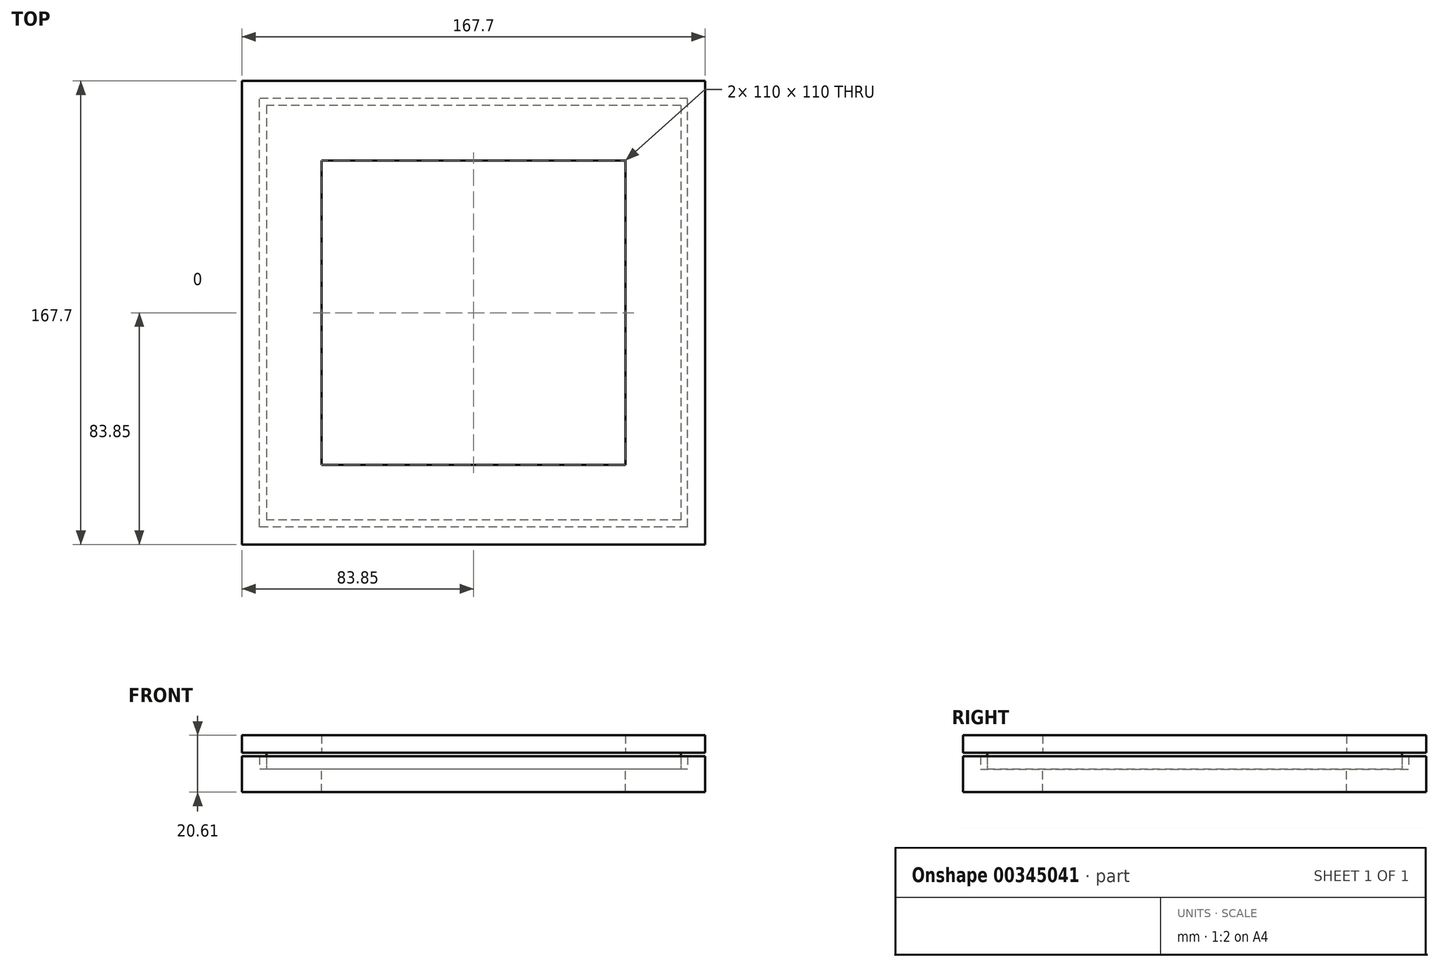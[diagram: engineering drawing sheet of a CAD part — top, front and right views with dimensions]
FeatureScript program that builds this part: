
annotation { "Feature Type Name" : "Feature", "Feature Type Description" : "" }
export const myFeature = defineFeature(function(context is Context, id is Id, definition is map)
    precondition{}
    {
        {
            var Q0;
            Q0=qCreatedBy(makeId("Top.planeOp"),FACE);
            var sketch = newSketch(context, id + "F0", { "sketchPlane" : qUnion([Q0])});
            skLineSegment(sketch, "E0.bottom", {"start": v(75, 75) * mm, "end": v(-75, 75) * mm});
            skLineSegment(sketch, "E0.top", {"start": v(75, -75) * mm, "end": v(-75, -75) * mm});
            skLineSegment(sketch, "E0.left", {"start": v(75, 75) * mm, "end": v(75, -75) * mm});
            skLineSegment(sketch, "E0.right", {"start": v(-75, 75) * mm, "end": v(-75, -75) * mm});
            skPoint(sketch, "E0.middle", {"position": v(0, 0) * mm});
            skSolve(sketch);
        }
        {
            var Q0;
            Q0 = qSketchRegion(id + "F0", true);
            extrude(context, id + "F1", {"entities" : qUnion([Q0]), "depth" : 6 * mm});
        }
        {
            var Q0;
            Q0=makeQuery(id+"F1.opExtrude","CAP_FACE",FACE,{"disambiguationData":[OSD([sQuery(id+"F0.wireOp",EDGE,"E0.bottom"),sQuery(id+"F0.wireOp",EDGE,"E0.top"),sQuery(id+"F0.wireOp",EDGE,"E0.left"),sQuery(id+"F0.wireOp",EDGE,"E0.right")])],"isStart":true});
            var sketch = newSketch(context, id + "F2", { "sketchPlane" : qUnion([Q0])});
            skLineSegment(sketch, "E1.bottom", {"start": v(55, 55) * mm, "end": v(-55, 55) * mm});
            skLineSegment(sketch, "E1.top", {"start": v(55, -55) * mm, "end": v(-55, -55) * mm});
            skLineSegment(sketch, "E1.left", {"start": v(55, 55) * mm, "end": v(55, -55) * mm});
            skLineSegment(sketch, "E1.right", {"start": v(-55, 55) * mm, "end": v(-55, -55) * mm});
            skPoint(sketch, "E1.middle", {"position": v(0, 0) * mm});
            skLineSegment(sketch, "E2.bottom", {"start": v(77.5, 77.5) * mm, "end": v(-77.5, 77.5) * mm});
            skLineSegment(sketch, "E2.top", {"start": v(77.5, -77.5) * mm, "end": v(-77.5, -77.5) * mm});
            skLineSegment(sketch, "E2.left", {"start": v(77.5, 77.5) * mm, "end": v(77.5, -77.5) * mm});
            skLineSegment(sketch, "E2.right", {"start": v(-77.5, 77.5) * mm, "end": v(-77.5, -77.5) * mm});
            skSolve(sketch);
        }
        {
            var Q0;
            Q0 = qSketchRegion(id + "F2", true);
            extrude(context, id + "F3", {"entities" : qUnion([Q0]), "depth" : 8.25 * mm});
        }
        {
            var Q0;
            Q0=makeQuery(id+"F3.opExtrude","CAP_FACE",FACE,{"disambiguationData":[OSD([sQuery(id+"F2.wireOp",EDGE,"E1.bottom"),sQuery(id+"F2.wireOp",EDGE,"E1.top"),sQuery(id+"F2.wireOp",EDGE,"E1.left"),sQuery(id+"F2.wireOp",EDGE,"E1.right"),sQuery(id+"F2.wireOp",EDGE,"E2.bottom"),sQuery(id+"F2.wireOp",EDGE,"E2.top"),sQuery(id+"F2.wireOp",EDGE,"E2.left"),sQuery(id+"F2.wireOp",EDGE,"E2.right")])],"isStart":false});
            var sketch = newSketch(context, id + "F4", { "sketchPlane" : qUnion([Q0])});
            skLineSegment(sketch, "E3.0", {"start": v(83.85, 83.85) * mm, "end": v(-83.85, 83.85) * mm});
            skLineSegment(sketch, "E3.1", {"start": v(83.85, 83.85) * mm, "end": v(83.85, -83.85) * mm});
            skLineSegment(sketch, "E3.2", {"start": v(83.85, -83.85) * mm, "end": v(-83.85, -83.85) * mm});
            skLineSegment(sketch, "E3.3", {"start": v(-83.85, 83.85) * mm, "end": v(-83.85, -83.85) * mm});
            skSolve(sketch);
        }
        {
            var Q0;
            Q0=makeQuery(id+"F4.imprint","IMPRINT",FACE,{"disambiguationData":[TD([[makeQuery(id+"F4.imprint","IMPRINT",EDGE,{"derivedFrom":sQuery(id+"F4.wireOp",EDGE,"E3.0")}),1.0]])]});
            extrude(context, id + "F5", {"entities" : qUnion([Q0]), "operationType" : NewBodyOperationType.ADD, "oppositeDirection" : true, "depth" : 12.95 * mm});
        }
        {
            var Q0;
            Q0=makeQuery(id+"F1.opExtrude","CAP_FACE",FACE,{"disambiguationData":[OSD([sQuery(id+"F0.wireOp",EDGE,"E0.bottom"),sQuery(id+"F0.wireOp",EDGE,"E0.top"),sQuery(id+"F0.wireOp",EDGE,"E0.left"),sQuery(id+"F0.wireOp",EDGE,"E0.right")])],"isStart":false});
            var sketch = newSketch(context, id + "F6", { "sketchPlane" : qUnion([Q0])});
            skLineSegment(sketch, "E4.bottom", {"start": v(83.85, 83.85) * mm, "end": v(-83.85, 83.85) * mm});
            skLineSegment(sketch, "E4.top", {"start": v(83.85, -83.85) * mm, "end": v(-83.85, -83.85) * mm});
            skLineSegment(sketch, "E4.left", {"start": v(83.85, 83.85) * mm, "end": v(83.85, -83.85) * mm});
            skLineSegment(sketch, "E4.right", {"start": v(-83.85, 83.85) * mm, "end": v(-83.85, -83.85) * mm});
            skPoint(sketch, "E4.middle", {"position": v(0, 0) * mm});
            skLineSegment(sketch, "E5.bottom", {"start": v(55, 55) * mm, "end": v(-55, 55) * mm});
            skLineSegment(sketch, "E5.top", {"start": v(55, -55) * mm, "end": v(-55, -55) * mm});
            skLineSegment(sketch, "E5.left", {"start": v(55, 55) * mm, "end": v(55, -55) * mm});
            skLineSegment(sketch, "E5.right", {"start": v(-55, 55) * mm, "end": v(-55, -55) * mm});
            skSolve(sketch);
        }
        {
            var Q0;
            Q0 = qSketchRegion(id + "F6", true);
            extrude(context, id + "F7", {"entities" : qUnion([Q0]), "depth" : 6.35 * mm});
        }
    });
